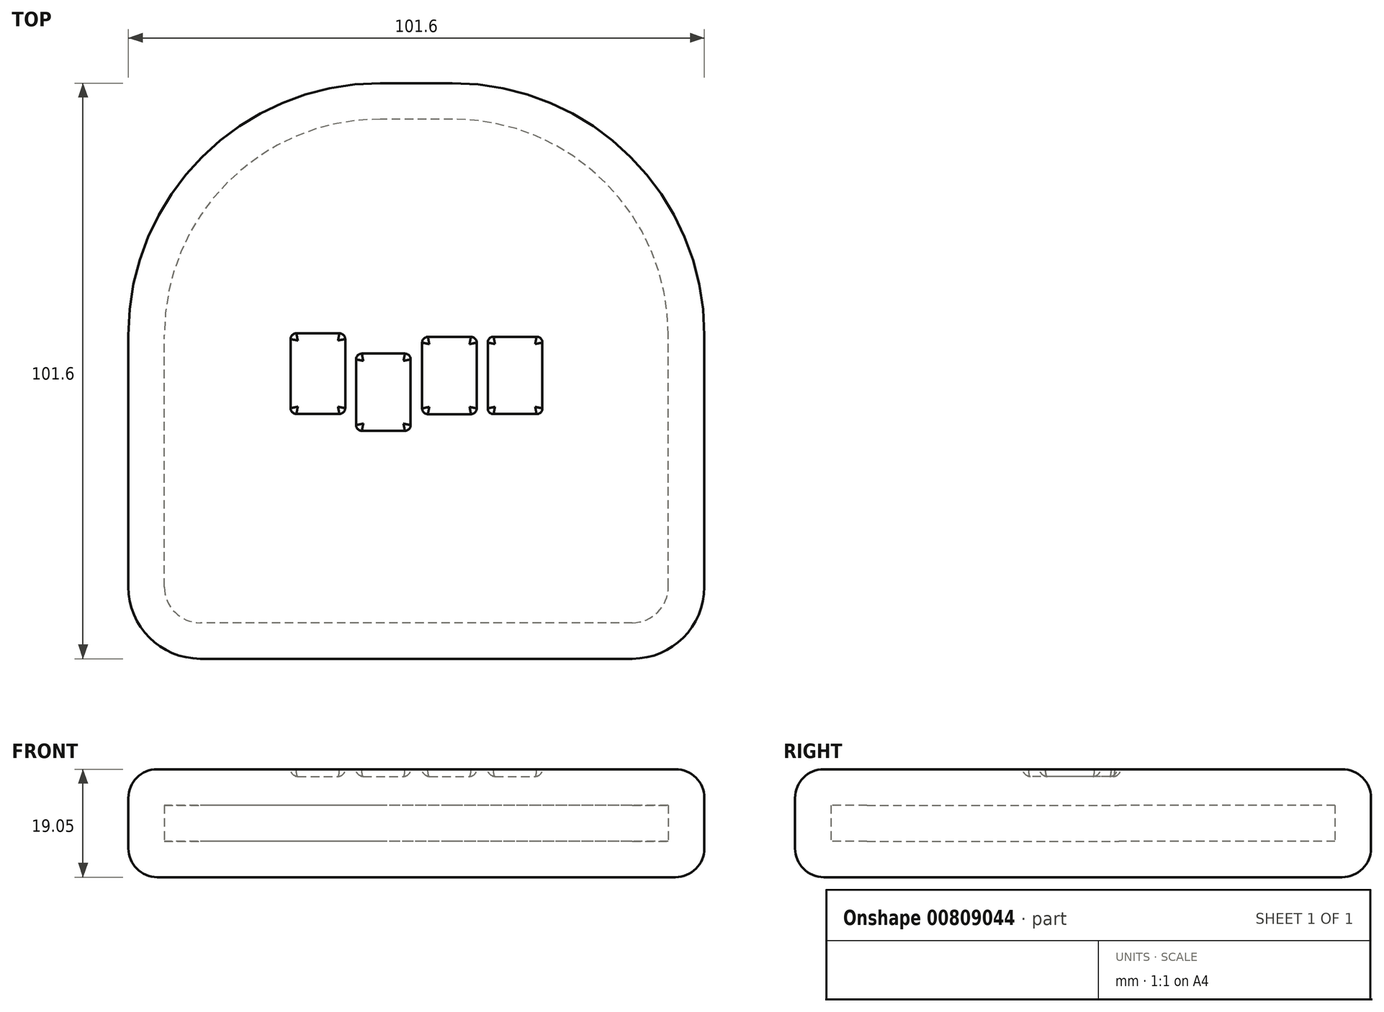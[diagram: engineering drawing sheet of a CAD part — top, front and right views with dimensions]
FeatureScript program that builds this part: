
annotation { "Feature Type Name" : "Feature", "Feature Type Description" : "" }
export const myFeature = defineFeature(function(context is Context, id is Id, definition is map)
    precondition{}
    {
        {
            var Q0;
            Q0=qCreatedBy(makeId("Top.planeOp"),FACE);
            cPlane(context, id + "F0", {"entities" : qUnion([Q0]), "cplaneType" : CPlaneType.OFFSET, "offset" : 6.35 * mm, "width" : 152.4 * mm, "height" : 152.4 * mm});
        }
        {
            var Q0;
            Q0=qCreatedBy(id+"F0.planeOp",FACE);
            var sketch = newSketch(context, id + "F1", { "sketchPlane" : qUnion([Q0])});
            skLineSegment(sketch, "E0.bottom", {"start": v(38.1, -44.45) * mm, "end": v(-38.1, -44.45) * mm});
            skLineSegment(sketch, "E0.top", {"start": v(6.35, 44.45) * mm, "end": v(-6.35, 44.45) * mm});
            skLineSegment(sketch, "E0.left", {"start": v(44.45, -38.1) * mm, "end": v(44.45, 6.35) * mm});
            skLineSegment(sketch, "E0.right", {"start": v(-44.45, -38.1) * mm, "end": v(-44.45, 6.35) * mm});
            skPoint(sketch, "E0.middle", {"position": v(0, 0) * mm});
            skPoint(sketch, "E1.visualSharp", {"position": v(-44.45, 44.45) * mm});
            skArc(sketch, "E1.filletArc", {"start": v(-6.35, 44.45) * mm, "mid": v(-33.3, 33.3) * mm, "end": v(-44.45, 6.35) * mm});
            skPoint(sketch, "E2.visualSharp", {"position": v(44.45, 44.45) * mm});
            skArc(sketch, "E2.filletArc", {"start": v(44.45, 6.35) * mm, "mid": v(33.3, 33.3) * mm, "end": v(6.35, 44.45) * mm});
            skPoint(sketch, "E3.visualSharp", {"position": v(-44.45, -44.45) * mm});
            skArc(sketch, "E3.filletArc", {"start": v(-44.45, -38.1) * mm, "mid": v(-42.6, -42.6) * mm, "end": v(-38.1, -44.45) * mm});
            skPoint(sketch, "E4.visualSharp", {"position": v(44.45, -44.45) * mm});
            skArc(sketch, "E4.filletArc", {"start": v(38.1, -44.45) * mm, "mid": v(42.6, -42.6) * mm, "end": v(44.45, -38.1) * mm});
            skSolve(sketch);
        }
        {
            var Q0;
            Q0=qCreatedBy(makeId("Top.planeOp"),FACE);
            var sketch = newSketch(context, id + "F2", { "sketchPlane" : qUnion([Q0])});
            skLineSegment(sketch, "E5.0", {"start": v(6.35, 50.8) * mm, "end": v(-6.35, 50.8) * mm});
            skArc(sketch, "E5.1", {"start": v(50.8, 6.35) * mm, "mid": v(37.78, 37.78) * mm, "end": v(6.35, 50.8) * mm});
            skArc(sketch, "E5.2", {"start": v(-6.35, 50.8) * mm, "mid": v(-37.78, 37.78) * mm, "end": v(-50.8, 6.35) * mm});
            skLineSegment(sketch, "E5.3", {"start": v(50.8, -38.1) * mm, "end": v(50.8, 6.35) * mm});
            skLineSegment(sketch, "E5.4", {"start": v(-50.8, -38.1) * mm, "end": v(-50.8, 6.35) * mm});
            skArc(sketch, "E5.5", {"start": v(-50.8, -38.1) * mm, "mid": v(-47.08, -47.08) * mm, "end": v(-38.1, -50.8) * mm});
            skLineSegment(sketch, "E5.6", {"start": v(38.1, -50.8) * mm, "end": v(-38.1, -50.8) * mm});
            skArc(sketch, "E5.7", {"start": v(38.1, -50.8) * mm, "mid": v(47.08, -47.08) * mm, "end": v(50.8, -38.1) * mm});
            skSolve(sketch);
        }
        {
            var Q0;
            Q0 = qSketchRegion(id + "F2", true);
            extrude(context, id + "F3", {"entities" : qUnion([Q0]), "depth" : 19.05 * mm, "offsetDistance" : 25.4 * mm});
        }
        {
            var Q0;
            Q0 = qSketchRegion(id + "F1", true);
            extrude(context, id + "F4", {"entities" : qUnion([Q0]), "operationType" : NewBodyOperationType.REMOVE, "depth" : 6.35 * mm, "offsetDistance" : 25.4 * mm});
        }
        {
            var Q0;
            Q0=makeQuery(id+"F3.opExtrude","CAP_EDGE",EDGE,{"disambiguationData":[OSD([sQuery(id+"F2.wireOp",EDGE,"E5.5")])],"isStart":false});
            fillet(context, id + "F5", {"entities" : qUnion([Q0]), "radius" : 5.08 * mm, "tangentPropagation" : true, "allowEdgeOverflow" : false});
        }
        {
            var Q0;
            Q0=makeQuery(id+"F3.opExtrude","CAP_EDGE",EDGE,{"disambiguationData":[OSD([sQuery(id+"F2.wireOp",EDGE,"E5.3")])],"isStart":true});
            fillet(context, id + "F6", {"entities" : qUnion([Q0]), "radius" : 5.08 * mm, "tangentPropagation" : true, "allowEdgeOverflow" : false});
        }
        {
            var Q0;
            Q0=qCreatedBy(makeId("Top.planeOp"),FACE);
            cPlane(context, id + "F7", {"entities" : qUnion([Q0]), "cplaneType" : CPlaneType.OFFSET, "offset" : 19.05 * mm, "width" : 152.4 * mm, "height" : 152.4 * mm});
        }
        {
            var Q0;
            Q0=qCreatedBy(id+"F7.planeOp",FACE);
            var sketch = newSketch(context, id + "F8", { "sketchPlane" : qUnion([Q0])});
            skLineSegment(sketch, "E6.bottom", {"start": v(-21.17, 6.64) * mm, "end": v(-13.57, 6.64) * mm});
            skLineSegment(sketch, "E6.top", {"start": v(-21.17, -7.6) * mm, "end": v(-13.57, -7.6) * mm});
            skLineSegment(sketch, "E6.left", {"start": v(-22.19, 5.62) * mm, "end": v(-22.19, -6.58) * mm});
            skLineSegment(sketch, "E6.right", {"start": v(-12.56, 5.62) * mm, "end": v(-12.56, -6.58) * mm});
            skPoint(sketch, "E7.visualSharp", {"position": v(-12.56, 6.64) * mm});
            skArc(sketch, "E7.filletArc", {"start": v(-12.56, 5.62) * mm, "mid": v(-12.85, 6.34) * mm, "end": v(-13.57, 6.64) * mm});
            skPoint(sketch, "E8.visualSharp", {"position": v(-22.19, 6.64) * mm});
            skArc(sketch, "E8.filletArc", {"start": v(-21.17, 6.64) * mm, "mid": v(-21.9, 6.34) * mm, "end": v(-22.19, 5.62) * mm});
            skPoint(sketch, "E9.visualSharp", {"position": v(-22.19, -7.6) * mm});
            skArc(sketch, "E9.filletArc", {"start": v(-22.19, -6.58) * mm, "mid": v(-21.9, -7.3) * mm, "end": v(-21.17, -7.6) * mm});
            skPoint(sketch, "E10.visualSharp", {"position": v(-12.56, -7.6) * mm});
            skArc(sketch, "E10.filletArc", {"start": v(-13.57, -7.6) * mm, "mid": v(-12.85, -7.3) * mm, "end": v(-12.56, -6.58) * mm});
            skLineSegment(sketch, "E11.bottom", {"start": v(-9.62, 3.05) * mm, "end": v(-2.02, 3.05) * mm});
            skLineSegment(sketch, "E11.top", {"start": v(-9.62, -10.58) * mm, "end": v(-2.02, -10.58) * mm});
            skLineSegment(sketch, "E11.left", {"start": v(-10.63, 2.04) * mm, "end": v(-10.63, -9.57) * mm});
            skLineSegment(sketch, "E11.right", {"start": v(-1, 2.04) * mm, "end": v(-1, -9.57) * mm});
            skArc(sketch, "E12.filletArc", {"start": v(-1, 2.04) * mm, "mid": v(-1.3, 2.75) * mm, "end": v(-2.02, 3.05) * mm});
            skArc(sketch, "E13.filletArc", {"start": v(-9.62, 3.05) * mm, "mid": v(-10.34, 2.75) * mm, "end": v(-10.63, 2.04) * mm});
            skArc(sketch, "E14.filletArc", {"start": v(-10.63, -9.57) * mm, "mid": v(-10.34, -10.28) * mm, "end": v(-9.62, -10.58) * mm});
            skArc(sketch, "E15.filletArc", {"start": v(-2.02, -10.58) * mm, "mid": v(-1.3, -10.28) * mm, "end": v(-1, -9.57) * mm});
            skLineSegment(sketch, "E16.bottom", {"start": v(2.03, 6) * mm, "end": v(9.63, 6) * mm});
            skLineSegment(sketch, "E16.top", {"start": v(2.03, -7.63) * mm, "end": v(9.63, -7.63) * mm});
            skLineSegment(sketch, "E16.left", {"start": v(1.02, 4.99) * mm, "end": v(1.02, -6.61) * mm});
            skLineSegment(sketch, "E16.right", {"start": v(10.65, 4.99) * mm, "end": v(10.65, -6.61) * mm});
            skArc(sketch, "E17.filletArc", {"start": v(10.65, 4.99) * mm, "mid": v(10.35, 5.7) * mm, "end": v(9.63, 6) * mm});
            skArc(sketch, "E18.filletArc", {"start": v(2.03, 6) * mm, "mid": v(1.31, 5.7) * mm, "end": v(1.02, 4.99) * mm});
            skArc(sketch, "E19.filletArc", {"start": v(1.02, -6.61) * mm, "mid": v(1.31, -7.33) * mm, "end": v(2.03, -7.63) * mm});
            skArc(sketch, "E20.filletArc", {"start": v(9.63, -7.63) * mm, "mid": v(10.35, -7.33) * mm, "end": v(10.65, -6.61) * mm});
            skLineSegment(sketch, "E21.bottom", {"start": v(13.61, 6.02) * mm, "end": v(21.21, 6.02) * mm});
            skLineSegment(sketch, "E21.top", {"start": v(13.61, -7.62) * mm, "end": v(21.21, -7.62) * mm});
            skLineSegment(sketch, "E21.left", {"start": v(12.6, 5) * mm, "end": v(12.6, -6.6) * mm});
            skLineSegment(sketch, "E21.right", {"start": v(22.23, 5) * mm, "end": v(22.23, -6.6) * mm});
            skArc(sketch, "E22.filletArc", {"start": v(22.23, 5) * mm, "mid": v(21.93, 5.72) * mm, "end": v(21.21, 6.02) * mm});
            skArc(sketch, "E23.filletArc", {"start": v(13.61, 6.02) * mm, "mid": v(12.9, 5.72) * mm, "end": v(12.6, 5) * mm});
            skArc(sketch, "E24.filletArc", {"start": v(12.6, -6.6) * mm, "mid": v(12.9, -7.32) * mm, "end": v(13.61, -7.62) * mm});
            skArc(sketch, "E25.filletArc", {"start": v(21.21, -7.62) * mm, "mid": v(21.93, -7.32) * mm, "end": v(22.23, -6.6) * mm});
            skSolve(sketch);
        }
        {
            var Q0;
            Q0=makeQuery(id+"F8.imprint","IMPRINT",FACE,{"disambiguationData":[TD([[makeQuery(id+"F8.imprint","IMPRINT",EDGE,{"derivedFrom":sQuery(id+"F8.wireOp",EDGE,"E6.bottom")}),-1.0]])]});
            var Q1;
            Q1=makeQuery(id+"F8.imprint","IMPRINT",FACE,{"disambiguationData":[TD([[makeQuery(id+"F8.imprint","IMPRINT",EDGE,{"derivedFrom":sQuery(id+"F8.wireOp",EDGE,"E11.bottom")}),-1.0]])]});
            var Q2;
            Q2=makeQuery(id+"F8.imprint","IMPRINT",FACE,{"disambiguationData":[TD([[makeQuery(id+"F8.imprint","IMPRINT",EDGE,{"derivedFrom":sQuery(id+"F8.wireOp",EDGE,"E16.bottom")}),-1.0]])]});
            var Q3;
            Q3=makeQuery(id+"F8.imprint","IMPRINT",FACE,{"disambiguationData":[TD([[makeQuery(id+"F8.imprint","IMPRINT",EDGE,{"derivedFrom":sQuery(id+"F8.wireOp",EDGE,"E21.bottom")}),-1.0]])]});
            extrude(context, id + "F9", {"entities" : qUnion([Q0, Q1, Q2, Q3]), "operationType" : NewBodyOperationType.REMOVE, "oppositeDirection" : true, "depth" : 1.27 * mm, "offsetDistance" : 25.4 * mm});
        }
        {
            var Q0;
            Q0=makeQuery(id+"F9.boolean.opBoolean","COPY",EDGE,{"derivedFrom":makeQuery(id+"F9.opExtrude","CAP_EDGE",EDGE,{"disambiguationData":[OSD([sQuery(id+"F8.wireOp",EDGE,"E6.bottom")])],"isStart":false})});
            var Q1;
            Q1=makeQuery(id+"F9.boolean.opBoolean","COPY",EDGE,{"derivedFrom":makeQuery(id+"F9.opExtrude","CAP_EDGE",EDGE,{"disambiguationData":[OSD([sQuery(id+"F8.wireOp",EDGE,"E11.bottom")])],"isStart":false})});
            var Q2;
            Q2=makeQuery(id+"F9.boolean.opBoolean","COPY",EDGE,{"derivedFrom":makeQuery(id+"F9.opExtrude","CAP_EDGE",EDGE,{"disambiguationData":[OSD([sQuery(id+"F8.wireOp",EDGE,"E16.bottom")])],"isStart":false})});
            var Q3;
            Q3=makeQuery(id+"F9.boolean.opBoolean","COPY",EDGE,{"derivedFrom":makeQuery(id+"F9.opExtrude","CAP_EDGE",EDGE,{"disambiguationData":[OSD([sQuery(id+"F8.wireOp",EDGE,"E21.bottom")])],"isStart":false})});
            fillet(context, id + "F10", {"entities" : qUnion([Q0, Q1, Q2, Q3]), "radius" : 1.27 * mm, "tangentPropagation" : true, "allowEdgeOverflow" : false});
        }
    });
